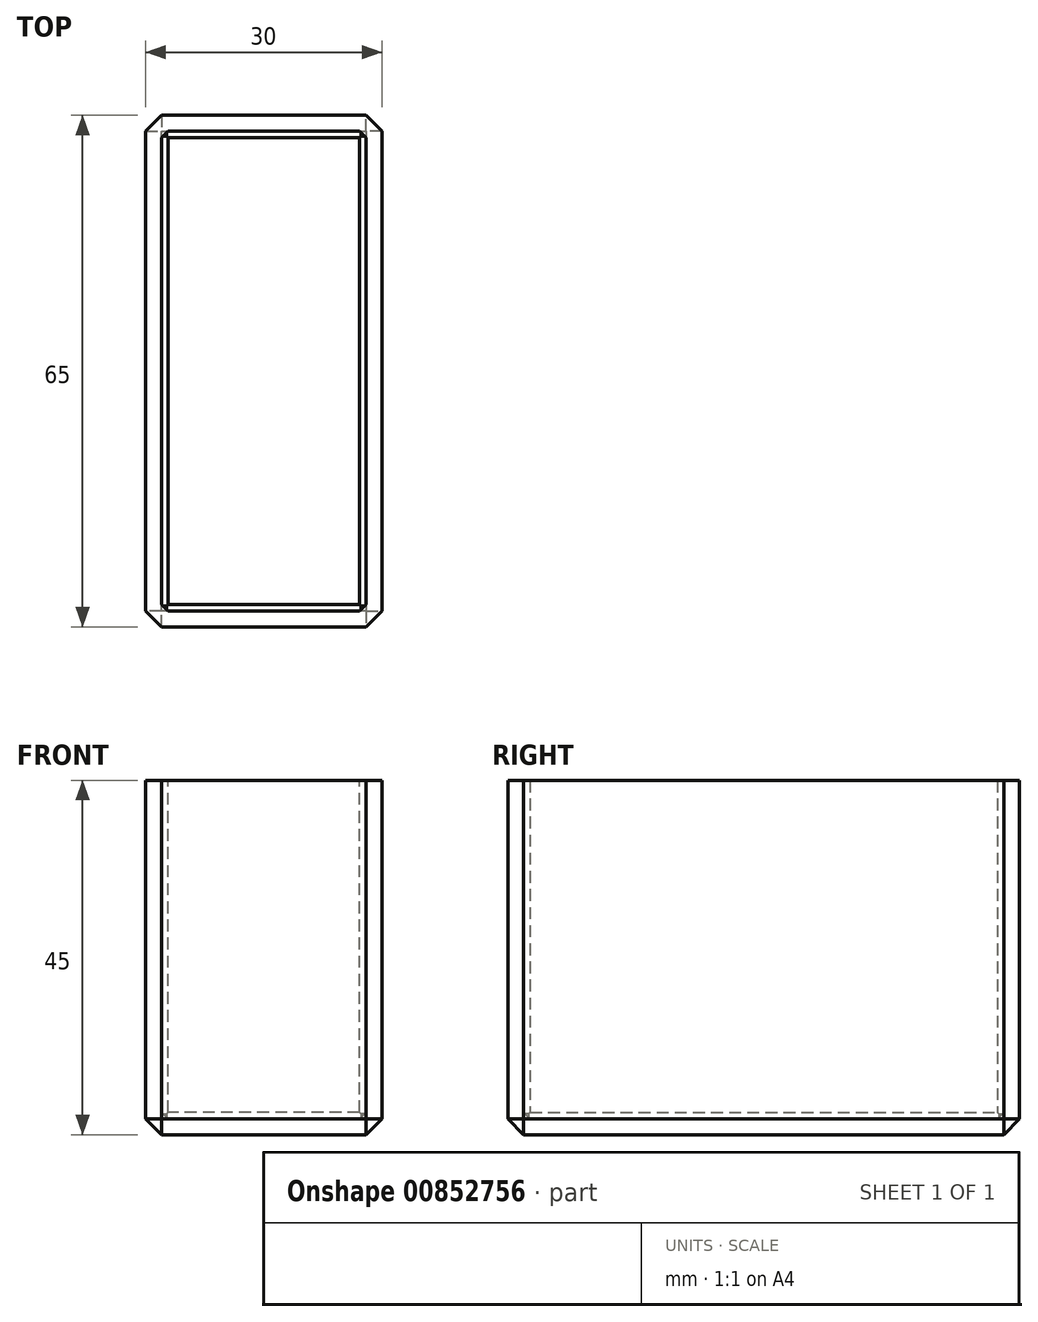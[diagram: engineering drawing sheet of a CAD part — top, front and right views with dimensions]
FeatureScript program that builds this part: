
annotation { "Feature Type Name" : "Feature", "Feature Type Description" : "" }
export const myFeature = defineFeature(function(context is Context, id is Id, definition is map)
    precondition{}
    {
        {
            var Q0;
            Q0=qCreatedBy(makeId("Top.planeOp"),FACE);
            var sketch = newSketch(context, id + "F0", { "sketchPlane" : qUnion([Q0])});
            skLineSegment(sketch, "E0.bottom", {"start": v(-15, 32.5) * mm, "end": v(15, 32.5) * mm});
            skLineSegment(sketch, "E0.top", {"start": v(-15, -32.5) * mm, "end": v(15, -32.5) * mm});
            skLineSegment(sketch, "E0.left", {"start": v(-15, 32.5) * mm, "end": v(-15, -32.5) * mm});
            skLineSegment(sketch, "E0.right", {"start": v(15, 32.5) * mm, "end": v(15, -32.5) * mm});
            skPoint(sketch, "E0.middle", {"position": v(0, 0) * mm});
            skSolve(sketch);
        }
        {
            var Q0;
            Q0=makeQuery(id+"F0.imprint","IMPRINT",FACE,{"disambiguationData":[TD([[makeQuery(id+"F0.imprint","IMPRINT",EDGE,{"derivedFrom":sQuery(id+"F0.wireOp",EDGE,"E0.bottom")}),-1.0]])]});
            extrude(context, id + "F1", {"entities" : qUnion([Q0]), "depth" : 45 * mm, "offsetDistance" : 25 * mm});
        }
        {
            var Q0;
            Q0=makeQuery(id+"F1.opExtrude","SWEPT_EDGE",EDGE,{"disambiguationData":[OSD([sQuery(id+"F0.wireOp",EDGE,"E0.top"),sQuery(id+"F0.wireOp",EDGE,"E0.right")])]});
            var Q1;
            Q1=makeQuery(id+"F1.opExtrude","SWEPT_EDGE",EDGE,{"disambiguationData":[OSD([sQuery(id+"F0.wireOp",EDGE,"E0.top"),sQuery(id+"F0.wireOp",EDGE,"E0.left")])]});
            var Q2;
            Q2=makeQuery(id+"F1.opExtrude","SWEPT_EDGE",EDGE,{"disambiguationData":[OSD([sQuery(id+"F0.wireOp",EDGE,"E0.bottom"),sQuery(id+"F0.wireOp",EDGE,"E0.right")])]});
            var Q3;
            Q3=makeQuery(id+"F1.opExtrude","SWEPT_EDGE",EDGE,{"disambiguationData":[OSD([sQuery(id+"F0.wireOp",EDGE,"E0.bottom"),sQuery(id+"F0.wireOp",EDGE,"E0.left")])]});
            var Q4;
            Q4=makeQuery(id+"F1.opExtrude","CAP_EDGE",EDGE,{"disambiguationData":[OSD([sQuery(id+"F0.wireOp",EDGE,"E0.right")])],"isStart":true});
            var Q5;
            Q5=makeQuery(id+"F1.opExtrude","CAP_EDGE",EDGE,{"disambiguationData":[OSD([sQuery(id+"F0.wireOp",EDGE,"E0.left")])],"isStart":true});
            var Q6;
            Q6=makeQuery(id+"F1.opExtrude","CAP_EDGE",EDGE,{"disambiguationData":[OSD([sQuery(id+"F0.wireOp",EDGE,"E0.bottom")])],"isStart":true});
            var Q7;
            Q7=makeQuery(id+"F1.opExtrude","CAP_EDGE",EDGE,{"disambiguationData":[OSD([sQuery(id+"F0.wireOp",EDGE,"E0.top")])],"isStart":true});
            chamfer(context, id + "F2", {"entities" : qUnion([Q0, Q1, Q2, Q3, Q4, Q5, Q6, Q7]), "width" : 2 * mm, "tangentPropagation" : true});
        }
        {
            var Q0;
            Q0=makeQuery(id+"F1.opExtrude","CAP_FACE",FACE,{"disambiguationData":[OSD([sQuery(id+"F0.wireOp",EDGE,"E0.bottom"),sQuery(id+"F0.wireOp",EDGE,"E0.top"),sQuery(id+"F0.wireOp",EDGE,"E0.left"),sQuery(id+"F0.wireOp",EDGE,"E0.right")])],"isStart":false});
            shell(context, id + "F3", {"entities" : qUnion([Q0]), "thickness" : 2 * mm});
        }
    });
